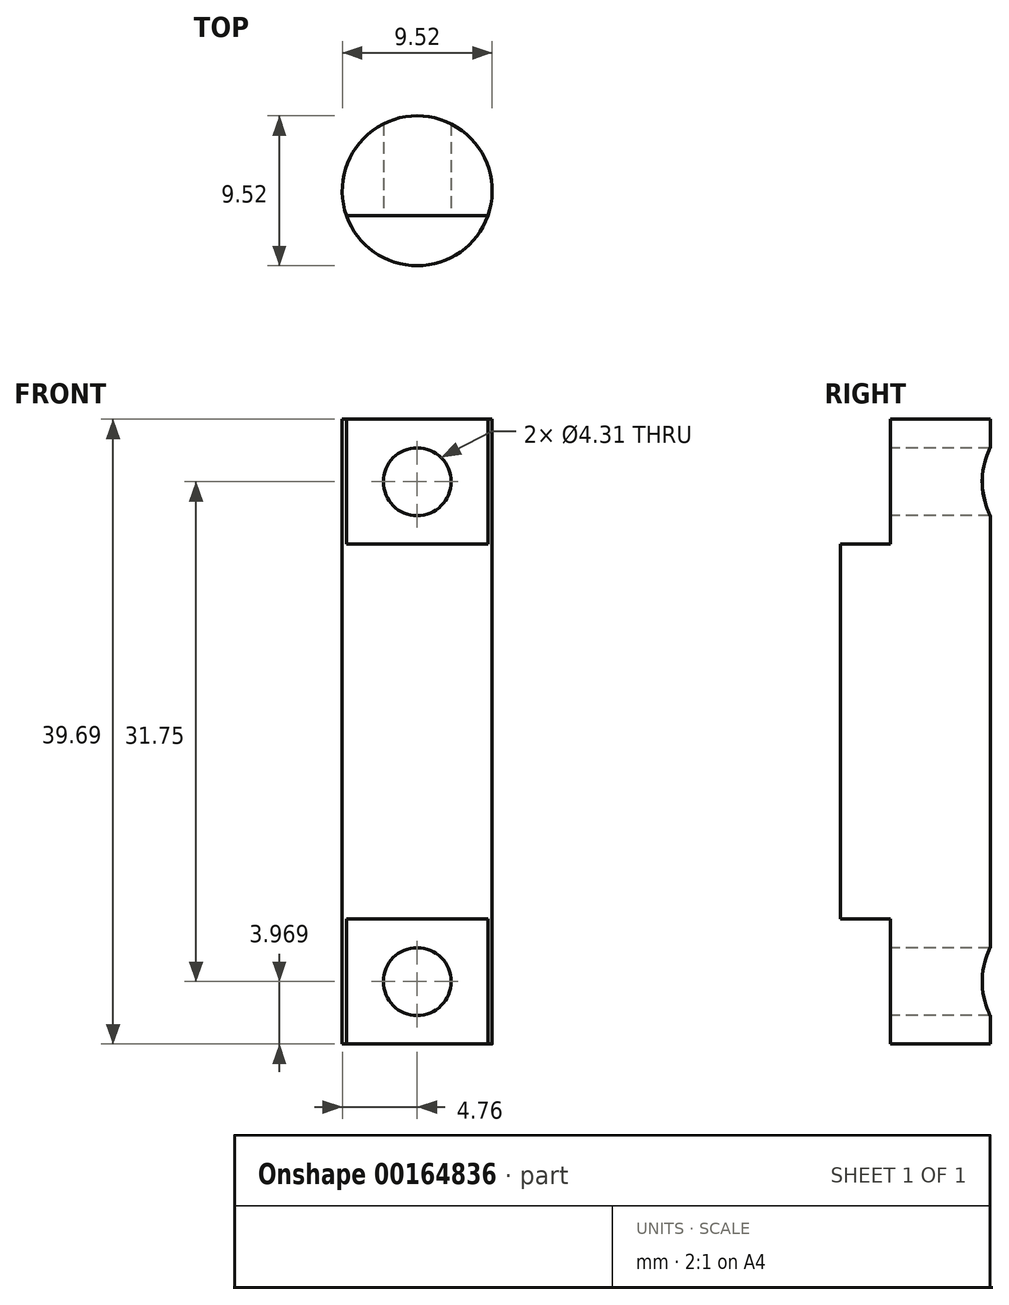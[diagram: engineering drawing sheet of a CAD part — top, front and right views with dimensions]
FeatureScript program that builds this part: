
annotation { "Feature Type Name" : "Feature", "Feature Type Description" : "" }
export const myFeature = defineFeature(function(context is Context, id is Id, definition is map)
    precondition{}
    {
        {
            var Q0;
            Q0=qCreatedBy(makeId("Top.planeOp"),FACE);
            var sketch = newSketch(context, id + "F0", { "sketchPlane" : qUnion([Q0])});
            skCircle(sketch, "E0", {"center": v(0, 0) * mm, "radius": 4.76 * mm});
            skSolve(sketch);
        }
        {
            var Q0;
            Q0=qSketchRegion(id+"F0",true);
            extrude(context, id + "F1", {"entities" : qUnion([Q0]), "depth" : 39.69 * mm});
        }
        {
            var Q0;
            Q0=makeQuery(id+"F1.opExtrude","CAP_FACE",FACE,{"disambiguationData":[OSD([sQuery(id+"F0.wireOp",EDGE,"E0")])],"isStart":false});
            var sketch = newSketch(context, id + "F2", { "sketchPlane" : qUnion([Q0])});
            skLineSegment(sketch, "E1.bottom", {"start": v(-4.5, -1.59) * mm, "end": v(4.5, -1.59) * mm});
            skLineSegment(sketch, "E1.top", {"start": v(-4.5, -4.76) * mm, "end": v(4.5, -4.76) * mm});
            skLineSegment(sketch, "E1.left", {"start": v(-4.5, -4.76) * mm, "end": v(-4.5, -1.59) * mm});
            skLineSegment(sketch, "E1.right", {"start": v(4.5, -4.76) * mm, "end": v(4.5, -1.59) * mm});
            skSolve(sketch);
        }
        {
            var Q0;
            Q0=qSketchRegion(id+"F2",true);
            extrude(context, id + "F3", {"entities" : qUnion([Q0]), "operationType" : NewBodyOperationType.REMOVE, "oppositeDirection" : true, "depth" : 7.94 * mm});
        }
        {
            var Q0;
            Q0=makeQuery(id+"F1.opExtrude","CAP_FACE",FACE,{"disambiguationData":[OSD([sQuery(id+"F0.wireOp",EDGE,"E0")])],"isStart":true});
            var sketch = newSketch(context, id + "F4", { "sketchPlane" : qUnion([Q0])});
            skLineSegment(sketch, "E2.bottom", {"start": v(-4.5, 1.59) * mm, "end": v(4.5, 1.59) * mm});
            skLineSegment(sketch, "E2.top", {"start": v(-4.5, 4.76) * mm, "end": v(4.5, 4.76) * mm});
            skLineSegment(sketch, "E2.left", {"start": v(-4.5, 1.59) * mm, "end": v(-4.5, 4.76) * mm});
            skLineSegment(sketch, "E2.right", {"start": v(4.5, 1.59) * mm, "end": v(4.5, 4.76) * mm});
            skSolve(sketch);
        }
        {
            var Q0;
            Q0=qSketchRegion(id+"F4",true);
            extrude(context, id + "F5", {"entities" : qUnion([Q0]), "operationType" : NewBodyOperationType.REMOVE, "oppositeDirection" : true, "depth" : 7.94 * mm});
        }
        {
            var Q0;
            Q0=makeQuery(id+"F5.boolean.opBoolean","COPY",FACE,{"derivedFrom":makeQuery(id+"F5.opExtrude","SWEPT_FACE",FACE,{"disambiguationData":[OSD([sQuery(id+"F4.wireOp",EDGE,"E2.bottom")])]})});
            var sketch = newSketch(context, id + "F6", { "sketchPlane" : qUnion([Q0])});
            skLineSegment(sketch, "E3", {"start": v(4.5, 35.72) * mm, "end": v(-4.5, 35.72) * mm, "construction": true});
            skCircle(sketch, "E4", {"center": v(0, 35.72) * mm, "radius": 2.15 * mm});
            skLineSegment(sketch, "E5", {"start": v(4.5, 3.97) * mm, "end": v(-4.5, 3.97) * mm, "construction": true});
            skCircle(sketch, "E6", {"center": v(0, 3.97) * mm, "radius": 2.15 * mm});
            skSolve(sketch);
        }
        {
            var Q0;
            Q0=qSketchRegion(id+"F6",true);
            var Q1;
            Q1=makeQuery(id+"F1.opExtrude","SWEPT_FACE",FACE,{"disambiguationData":[OSD([sQuery(id+"F0.wireOp",EDGE,"E0")])]});
            extrude(context, id + "F7", {"entities" : qUnion([Q0]), "operationType" : NewBodyOperationType.REMOVE, "endBound" : BoundingType.UP_TO_SURFACE, "oppositeDirection" : true, "endBoundEntityFace" : qUnion([Q1]), "depth" : 25.4 * mm});
        }
    });
